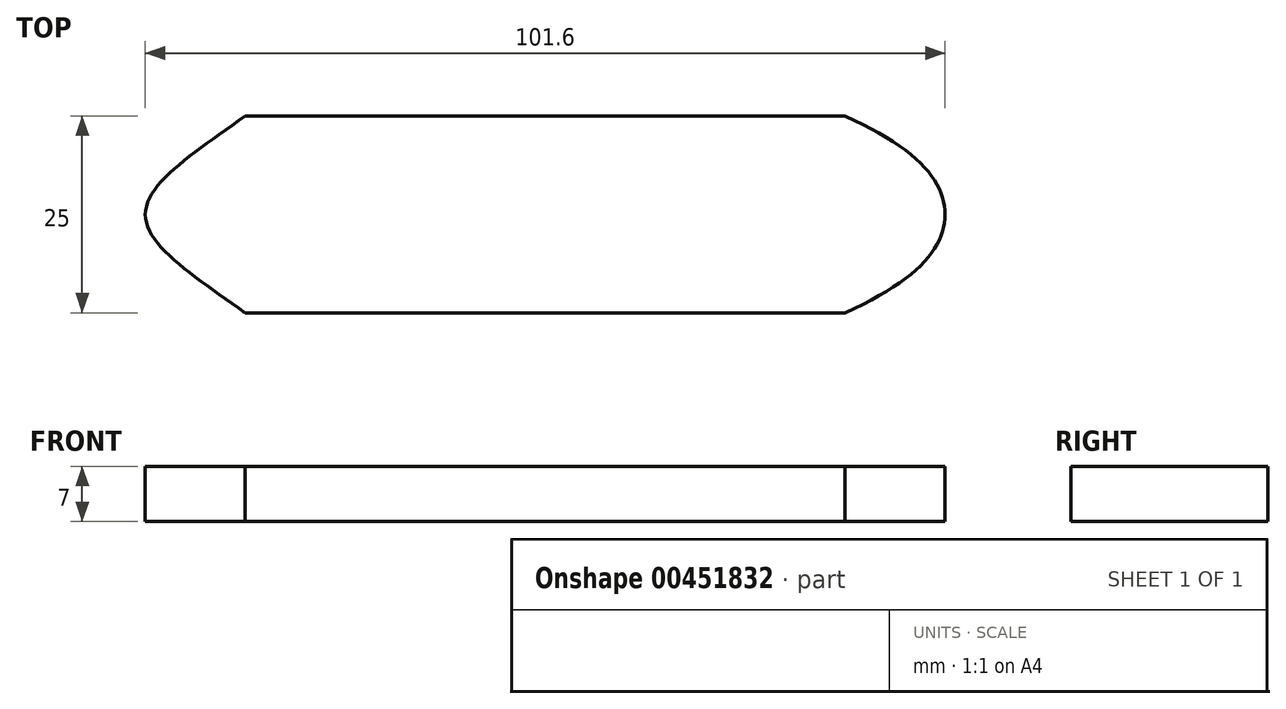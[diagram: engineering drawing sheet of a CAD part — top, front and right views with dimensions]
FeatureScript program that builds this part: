
annotation { "Feature Type Name" : "Feature", "Feature Type Description" : "" }
export const myFeature = defineFeature(function(context is Context, id is Id, definition is map)
    precondition{}
    {
        {
            var Q0;
            Q0=qCreatedBy(makeId("Top.planeOp"),FACE);
            var sketch = newSketch(context, id + "F0", { "sketchPlane" : qUnion([Q0])});
            skLineSegment(sketch, "E0.bottom", {"start": v(38.1, 12.5) * mm, "end": v(-38.1, 12.5) * mm});
            skLineSegment(sketch, "E0.top", {"start": v(38.1, -12.5) * mm, "end": v(-38.1, -12.5) * mm});
            skLineSegment(sketch, "E0.left", {"start": v(38.1, 12.5) * mm, "end": v(38.1, -12.5) * mm});
            skLineSegment(sketch, "E0.right", {"start": v(-38.1, 12.5) * mm, "end": v(-38.1, -12.5) * mm});
            skPoint(sketch, "E0.middle", {"position": v(0, 0) * mm});
            skFitSpline(sketch, "E1", {"points": [v(-38.1, 12.5) * mm, v(-50.8, 0) * mm, v(-38.1, -12.5) * mm], "startDerivative": vector(-38.35, -27.28) * mm, "endDerivative": vector(38.35, -27.28) * mm});
            skFitSpline(sketch, "E2", {"points": [v(38.1, 12.5) * mm, v(50.8, 0) * mm, v(38.1, -12.5) * mm], "startDerivative": vector(55.6, -25) * mm, "endDerivative": vector(-55.6, -25) * mm});
            skLineSegment(sketch, "E3", {"start": v(-50.8, 0) * mm, "end": v(-38.1, 0) * mm});
            skLineSegment(sketch, "E4", {"start": v(38.1, 0) * mm, "end": v(50.8, 0) * mm});
            skSolve(sketch);
        }
        {
            var Q0;
            Q0 = qSketchRegion(id + "F0", true);
            extrude(context, id + "F1", {"entities" : qUnion([Q0]), "depth" : 7 * mm});
        }
    });
